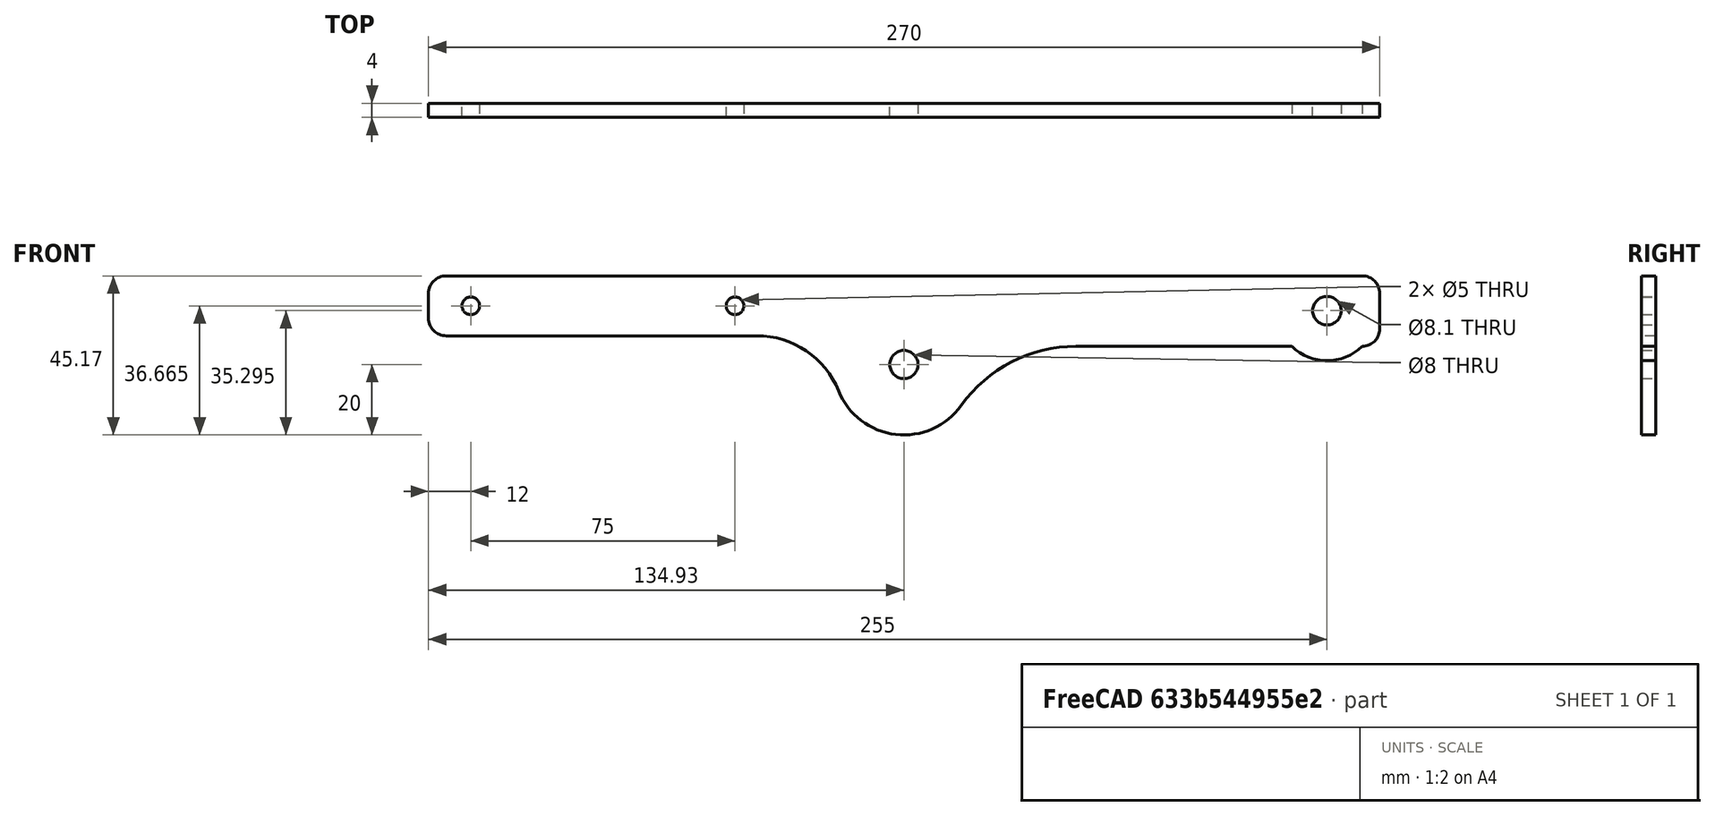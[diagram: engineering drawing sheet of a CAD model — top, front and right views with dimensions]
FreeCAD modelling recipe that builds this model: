
FCSTD DOCUMENT  (FreeCAD 0.17R13519 (Git))
Label: Balancin
License: All rights reserved
LicenseURL: http://en.wikipedia.org/wiki/All_rights_reserved
objects: Sketcher::SketchObject×1, PartDesign::Pad×1, PartDesign::Body×1
note: 4 computed .brp shape members not serialized (recipe doc carries the construction recipe); baked Part::Feature solids carry a one-line shape summary decoded from their .brp

FEATURE [Sketcher::SketchObject] Sketch
  MapMode = 5
  Placement = pos=(0,0,0) rot=(1,0,0;1.5708rad)
  Support = -> [XZ_Plane]
  sketch-geometry (21):
    g0: LineSegment StartX=-134.93 StartY=13.1651 StartZ=0 EndX=-134.93 EndY=20.1651 EndZ=0
    g1: LineSegment StartX=-129.93 StartY=25.1651 StartZ=0 EndX=130.07 EndY=25.1651 EndZ=0
    g2: LineSegment StartX=135.07 StartY=20.1651 StartZ=0 EndX=135.07 EndY=10.1651 EndZ=0
    g3: LineSegment StartX=130.07 StartY=5.16508 StartZ=0 EndX=130.024 EndY=5.16508 EndZ=0
    g4: LineSegment StartX=110.116 StartY=5.16508 StartZ=0 EndX=48.8521 EndY=5.16508 EndZ=0
    g5: LineSegment StartX=-129.93 StartY=8.16508 StartZ=0 EndX=-41.7323 EndY=8.16508 EndZ=0
    g6: Circle CenterX=0 CenterY=0 CenterZ=0 NormalX=0 NormalY=0 NormalZ=1 AngleXU=0 Radius=4
    g7: ArcOfCircle CenterX=0 CenterY=0 CenterZ=0 NormalX=0 NormalY=0 NormalZ=1 AngleXU=0 Radius=20 StartAngle=3.52503 EndAngle=5.66374
    g8: ArcOfCircle CenterX=120.07 CenterY=15.2951 CenterZ=0 NormalX=0 NormalY=0 NormalZ=1 AngleXU=0 Radius=14.202 StartAngle=3.93576 EndAngle=5.48902
    g9: Circle CenterX=120.07 CenterY=15.2951 CenterZ=0 NormalX=0 NormalY=0 NormalZ=1 AngleXU=0 Radius=4.05
    g10: Circle CenterX=-122.93 CenterY=16.6651 CenterZ=0 NormalX=0 NormalY=0 NormalZ=1 AngleXU=0 Radius=2.5
    g11: Circle CenterX=-47.93 CenterY=16.6651 CenterZ=0 NormalX=0 NormalY=0 NormalZ=1 AngleXU=0 Radius=2.5
    g12: ArcOfCircle CenterX=48.8521 CenterY=-34.8349 CenterZ=0 NormalX=0 NormalY=0 NormalZ=1 AngleXU=0 Radius=40 StartAngle=1.5708 EndAngle=2.52215
    g13: ArcOfCircle CenterX=-41.7323 CenterY=-16.8349 CenterZ=0 NormalX=0 NormalY=0 NormalZ=1 AngleXU=0 Radius=25 StartAngle=0.383436 EndAngle=1.5708
    g14: ArcOfCircle CenterX=-129.93 CenterY=13.1651 CenterZ=0 NormalX=0 NormalY=0 NormalZ=1 AngleXU=0 Radius=5 StartAngle=3.14159 EndAngle=4.71239
    g15: ArcOfCircle CenterX=-129.93 CenterY=20.1651 CenterZ=0 NormalX=0 NormalY=0 NormalZ=1 AngleXU=0 Radius=5 StartAngle=1.5708 EndAngle=3.14159
    g16: ArcOfCircle CenterX=130.07 CenterY=20.1651 CenterZ=0 NormalX=0 NormalY=0 NormalZ=1 AngleXU=0 Radius=5 StartAngle=0 EndAngle=1.5708
    g17: ArcOfCircle CenterX=130.07 CenterY=10.1651 CenterZ=0 NormalX=0 NormalY=0 NormalZ=1 AngleXU=0 Radius=5 StartAngle=4.71239 EndAngle=6.28319
    g18: LineSegment [constr] StartX=-134.93 StartY=16.6651 StartZ=0 EndX=135.07 EndY=16.6651 EndZ=0
    g19: LineSegment [constr] StartX=130.07 StartY=5.16508 StartZ=0 EndX=110.116 EndY=5.16508 EndZ=0
    g20: LineSegment [constr] StartX=-41.7323 StartY=-16.8349 StartZ=0 EndX=-41.7323 EndY=8.16508 EndZ=0
  constraints (57):
    c: Vertical(g0)
    c: Horizontal(g1)
    c: Vertical(g2)
    c: Horizontal(g3)
    c: Horizontal(g4)
    c: Horizontal(g5)
    c: Coincident(g6,g-1)
    c: Coincident(g7,g6)
    c: Coincident(g9,g8)
    c: Coincident(g8,g3)
    c: Coincident(g8,g4)
    c: Tangent(g7,g12) = 1.5708
    c: PointOnObject(g12,g4)
    c: Tangent(g5,g14) = -1.5708
    c: Tangent(g0,g14) = 1.5708
    c: Tangent(g0,g15) = 1.5708
    c: Tangent(g1,g15) = 1.5708
    c: Tangent(g2,g16) = 1.5708
    c: Tangent(g1,g16) = 1.5708
    c: Tangent(g3,g17) = 1.5708
    c: Tangent(g2,g17) = 1.5708
    c: Equal(g17,g16)
    c: Equal(g16,g14)
    c: Equal(g14,g15)
    c: Radius(g15) = 5
    c: Equal(g10,g11)
    c: Radius(g13) = 25
    c: Radius(g7) = 20
    c: Radius(g12) = 40
    c: Coincident(g13,g5)
    c: Tangent(g4,g12)
    c: PointOnObject(g4,g12)
    c: DistanceY(g2,g2) = 10
    c: Radius(g9) = 4.05
    c: Radius(g6) = 4
    c: PointOnObject(g18,g2)
    c: Horizontal(g18)
    c: DistanceX(g18,g18) = 270
    c: Tangent(g13,g7) = 1.5708
    c: Symmetric(g0,g0,g18)
    c: PointOnObject(g10,g18)
    c: PointOnObject(g11,g18)
    c: Radius(g8) = 14.202
    c: DistanceY(g8,g1) = 9.87
    c: DistanceX(g8,g2) = 15
    c: DistanceX(g10,g11) = 75
    c: DistanceX(g11,g6) = 47.93
    c: DistanceX(g0,g10) = 12
    c: Coincident(g19,g3)
    c: Horizontal(g19)
    c: Coincident(g19,g4)
    c: DistanceY(g0,g0) = 7
    c: DistanceX(g4,g4) = 61.264
    c: Coincident(g20,g13)
    c: Vertical(g20)
    c: Coincident(g20,g5)
    c: Radius(g11) = 2.5
FEATURE [PartDesign::Pad] Pad
  Length = 4
  Length2 = 100
  Placement = pos=(0,0,0) rot=(1,0,0;1.5708rad)
  Profile = -> Sketch
  Type = 0
FEATURE [PartDesign::Body] Body
  Group = -> [Sketch,Pad]
  Origin = -> Origin
  Tip = -> Pad
